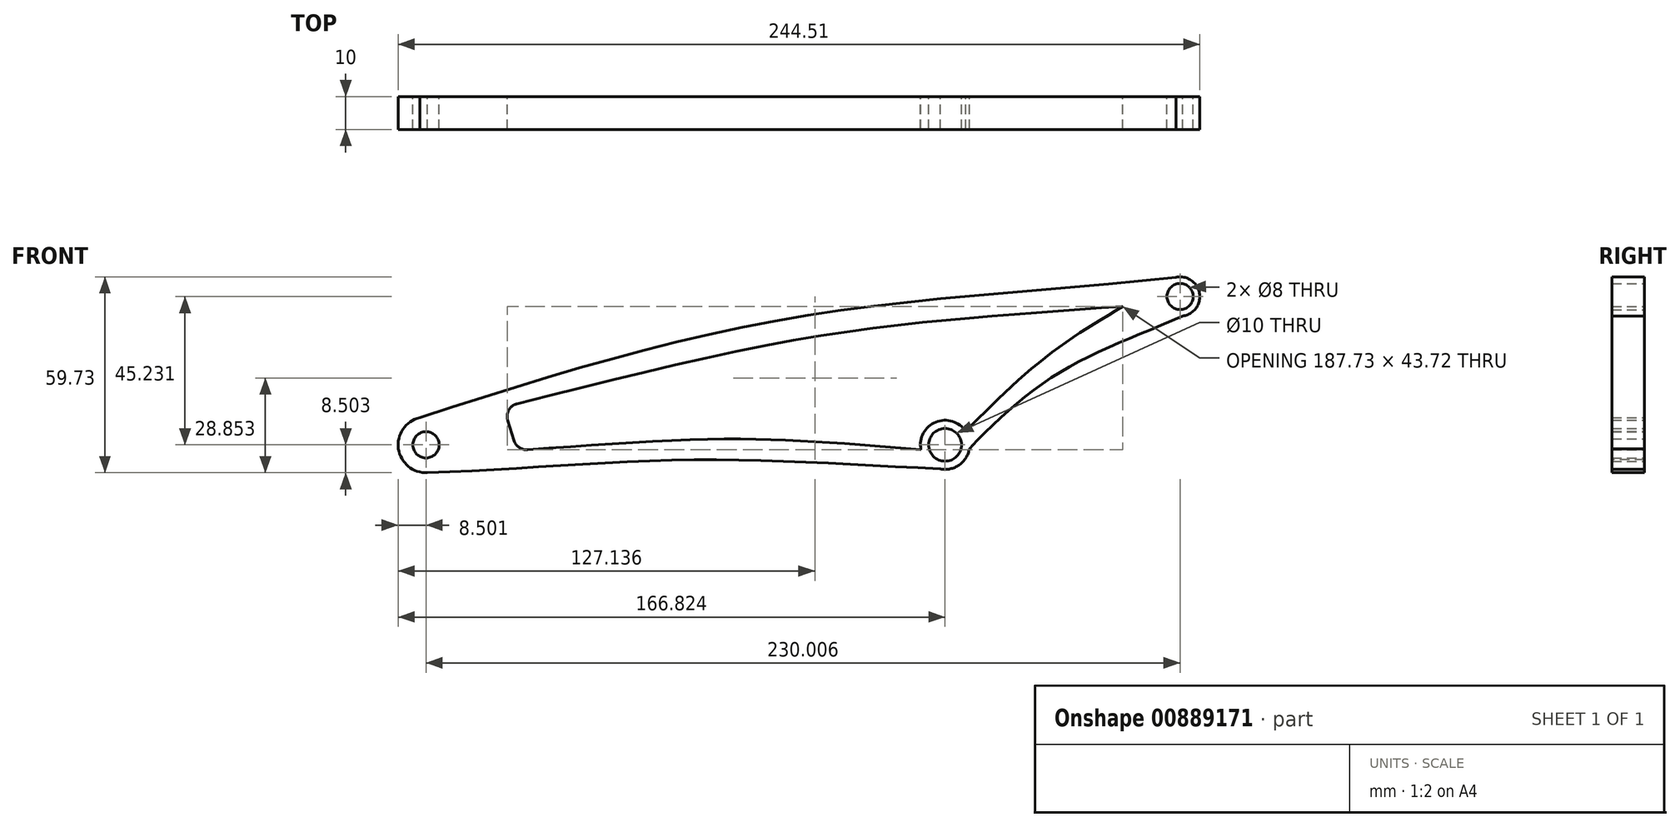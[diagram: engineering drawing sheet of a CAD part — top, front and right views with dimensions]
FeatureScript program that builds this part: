
annotation { "Feature Type Name" : "Feature", "Feature Type Description" : "" }
export const myFeature = defineFeature(function(context is Context, id is Id, definition is map)
    precondition{}
    {
        {
            var Q0;
            Q0=qCreatedBy(makeId("Front.planeOp"),FACE);
            var sketch = newSketch(context, id + "F0", { "sketchPlane" : qUnion([Q0])});
            skCircle(sketch, "E0", {"center": v(100.68, 28.62) * mm, "radius": 4 * mm});
            skCircle(sketch, "E1", {"center": v(29, -16.6) * mm, "radius": 5 * mm});
            skCircle(sketch, "E2", {"center": v(-129.33, -16.6) * mm, "radius": 4 * mm});
            skCircle(sketch, "E3", {"center": v(-129.33, -16.6) * mm, "radius": 8.5 * mm});
            skCircle(sketch, "E4", {"center": v(29, -16.6) * mm, "radius": 7.5 * mm});
            skCircle(sketch, "E5", {"center": v(100.68, 28.62) * mm, "radius": 6 * mm});
            skFitSpline(sketch, "E6", {"points": [v(100.68, 34.62) * mm, v(-17.5, 22.13) * mm, v(-131.25, -8.33) * mm], "startDerivative": vector(-237.07, -26.21) * mm, "endDerivative": vector(-225.05, -73.35) * mm});
            skFitSpline(sketch, "E7", {"points": [v(101.43, 22.67) * mm, v(64.84, 6) * mm, v(36.4, -17.78) * mm], "startDerivative": vector(-75.34, -33.08) * mm, "endDerivative": vector(-53.86, -56.97) * mm});
            skFitSpline(sketch, "E8", {"points": [v(29.7, -24.07) * mm, v(-50.17, -21.23) * mm, v(-128.88, -25.1) * mm], "startDerivative": vector(-159.47, 7.96) * mm, "endDerivative": vector(-157.97, -4.92) * mm});
            skFitSpline(sketch, "E9", {"points": [v(83.17, 25.6) * mm, v(59.35, 9.88) * mm, v(35.26, -12.48) * mm], "startDerivative": vector(-50.07, -30.03) * mm, "endDerivative": vector(-45.8, -45.93) * mm});
            skFitSpline(sketch, "E10", {"points": [v(21.63, -18.03) * mm, v(-10.83, -15.61) * mm, v(-44.19, -14.9) * mm, v(-101.5, -18.35) * mm], "startDerivative": vector(-109.97, 8.96) * mm, "endDerivative": vector(-154.27, -11.57) * mm});
            skLineSegment(sketch, "E11", {"start": v(-102.45, -15.33) * mm, "end": v(-104.4, -9.17) * mm});
            skFitSpline(sketch, "E12", {"points": [v(83.17, 25.6) * mm, v(39.74, 22.37) * mm, v(-17.44, 15.22) * mm, v(-105.67, -5.13) * mm], "startDerivative": vector(-152.71, -10.51) * mm, "endDerivative": vector(-230.23, -58.26) * mm});
            skArc(sketch, "E13.filletArc", {"start": v(-101.56, -4.1) * mm, "mid": v(-104.07, -6.02) * mm, "end": v(-104.4, -9.17) * mm});
            skArc(sketch, "E14.filletArc", {"start": v(-102.45, -15.33) * mm, "mid": v(-100.88, -17.44) * mm, "end": v(-98.34, -18.12) * mm});
            skSolve(sketch);
        }
        {
            var Q0;
            Q0 = qSketchRegion(id + "F0", true);
            extrude(context, id + "F1", {"entities" : qUnion([Q0]), "depth" : 10 * mm, "offsetDistance" : 25 * mm});
        }
    });
